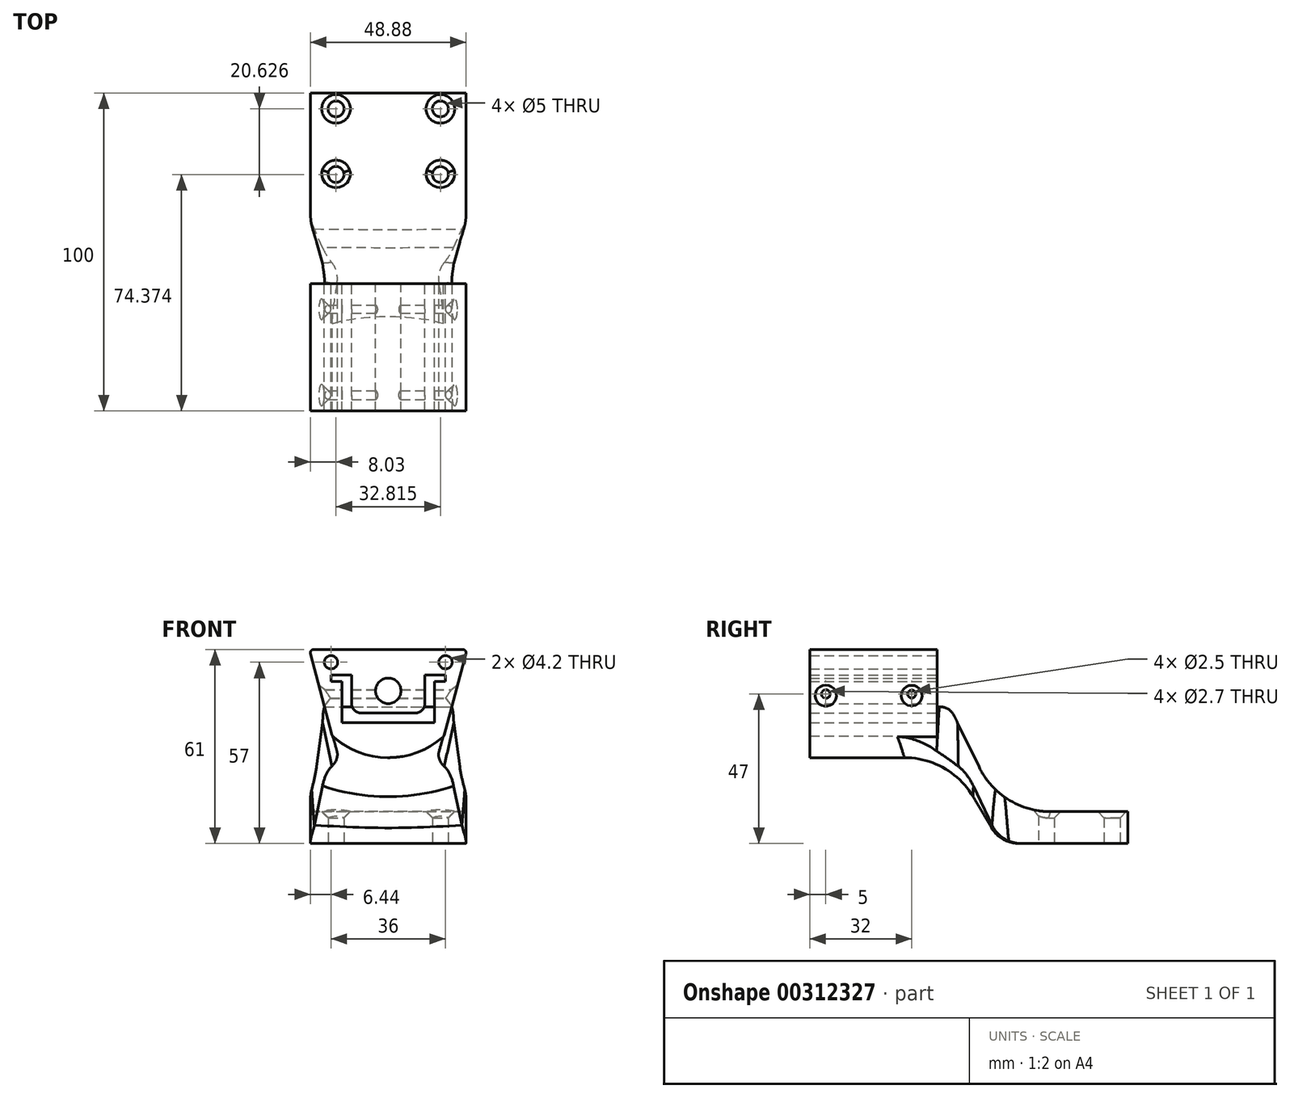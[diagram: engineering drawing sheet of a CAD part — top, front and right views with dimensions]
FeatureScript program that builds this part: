
annotation { "Feature Type Name" : "Feature", "Feature Type Description" : "" }
export const myFeature = defineFeature(function(context is Context, id is Id, definition is map)
    precondition{}
    {
        {
            var Q0;
            Q0=qCreatedBy(makeId("Front.planeOp"),FACE);
            var sketch = newSketch(context, id + "F0", { "sketchPlane" : qUnion([Q0])});
            skLineSegment(sketch, "E0", {"start": v(11.5, -9) * mm, "end": v(11.5, 0) * mm});
            skLineSegment(sketch, "E1", {"start": v(11.5, 0) * mm, "end": v(18, 0) * mm});
            skLineSegment(sketch, "E2", {"start": v(18, 0) * mm, "end": v(18, -2) * mm});
            skLineSegment(sketch, "E3", {"start": v(18, -2) * mm, "end": v(14.5, -2) * mm});
            skLineSegment(sketch, "E4", {"start": v(14.5, -2) * mm, "end": v(14.5, -15) * mm});
            skLineSegment(sketch, "E5", {"start": v(24.74, 8) * mm, "end": v(0.02, 8) * mm});
            skLineSegment(sketch, "E6.MirrorCS", {"start": v(-11.5, -9) * mm, "end": v(-11.5, 0) * mm});
            skLineSegment(sketch, "E7.MirrorCS", {"start": v(-11.5, 0) * mm, "end": v(-18, 0) * mm});
            skLineSegment(sketch, "E8.MirrorCS", {"start": v(-14.5, -2) * mm, "end": v(-14.5, -15) * mm});
            skLineSegment(sketch, "E9.MirrorCS", {"start": v(-14.98, 8) * mm, "end": v(0.02, 8) * mm});
            skLineSegment(sketch, "E10.MirrorCS", {"start": v(-18, 0) * mm, "end": v(-18, -2) * mm});
            skLineSegment(sketch, "E11.MirrorCS", {"start": v(-18, -2) * mm, "end": v(-14.5, -2) * mm});
            skPoint(sketch, "E12.visualSharp", {"position": v(11.5, -12) * mm});
            skArc(sketch, "E12.filletArc", {"start": v(8.5, -12) * mm, "mid": v(10.62, -11.12) * mm, "end": v(11.5, -9) * mm});
            skPoint(sketch, "E13.visualSharp", {"position": v(-11.5, -12) * mm});
            skArc(sketch, "E13.filletArc", {"start": v(-11.5, -9) * mm, "mid": v(-10.62, -11.12) * mm, "end": v(-8.5, -12) * mm});
            skPoint(sketch, "E14.visualSharp", {"position": v(-20.98, 8) * mm});
            skPoint(sketch, "E15.visualSharp", {"position": v(21.02, 8) * mm});
            skCircle(sketch, "E16", {"center": v(0, 0) * mm, "radius": 26 * mm, "construction": true});
            skLineSegment(sketch, "E17", {"start": v(17.5, -19.23) * mm, "end": v(24.74, 8) * mm});
            skLineSegment(sketch, "E18", {"start": v(-14.98, 8) * mm, "end": v(-24.74, 8) * mm});
            skLineSegment(sketch, "E19", {"start": v(-24.74, 8) * mm, "end": v(-17.64, -19.1) * mm});
            skLineSegment(sketch, "E20", {"start": v(-8.5, -12) * mm, "end": v(8.5, -12) * mm});
            skCircle(sketch, "E21", {"center": v(0, -5) * mm, "radius": 4 * mm});
            skCircle(sketch, "E22", {"center": v(-18, 4) * mm, "radius": 2.1 * mm});
            skCircle(sketch, "E23", {"center": v(18, 4) * mm, "radius": 2.1 * mm});
            skArc(sketch, "E24", {"start": v(17.5, -19.23) * mm, "mid": v(-0.1, -26) * mm, "end": v(-17.64, -19.1) * mm});
            skLineSegment(sketch, "E25", {"start": v(-14.5, -15) * mm, "end": v(14.5, -15) * mm});
            skSolve(sketch);
        }
        {
            var Q0;
            Q0=qSketchRegion(id+"F0",true);
            extrude(context, id + "F1", {"entities" : qUnion([Q0]), "depth" : 40 * mm});
        }
        {
            var Q0;
            Q0=qCreatedBy(makeId("Right.planeOp"),FACE);
            var sketch = newSketch(context, id + "F2", { "sketchPlane" : qUnion([Q0])});
            skCircle(sketch, "E26", {"center": v(-35, -6) * mm, "radius": 1.35 * mm});
            skCircle(sketch, "E27", {"center": v(-8, -6) * mm, "radius": 1.25 * mm});
            skSolve(sketch);
        }
        {
            var Q0;
            Q0=qSketchRegion(id+"F2",true);
            extrude(context, id + "F3", {"entities" : qUnion([Q0]), "operationType" : NewBodyOperationType.REMOVE, "endBound" : BoundingType.THROUGH_ALL, "oppositeDirection" : true, "depth" : 25 * mm, "hasSecondDirection" : true, "secondDirectionBound" : SecondDirectionBoundingType.THROUGH_ALL, "secondDirectionOppositeDirection" : false, "secondDirectionDepth" : 25 * mm});
        }
        {
            var Q0;
            Q0=makeQuery(id+"F3.boolean.opBoolean","INTERSECT",EDGE,{"derivedFrom":[makeQuery(id+"F1.opExtrude","SWEPT_FACE",FACE,{"disambiguationData":[OSD([sQuery(id+"F0.wireOp",EDGE,"E17")])]}),makeQuery(id+"F3.opExtrude","SWEPT_FACE",FACE,{"disambiguationData":[OSD([sQuery(id+"F2.wireOp",EDGE,"E26")])]})]});
            var Q1;
            Q1=makeQuery(id+"F3.boolean.opBoolean","INTERSECT",EDGE,{"derivedFrom":[makeQuery(id+"F1.opExtrude","SWEPT_FACE",FACE,{"disambiguationData":[OSD([sQuery(id+"F0.wireOp",EDGE,"E19")])]}),makeQuery(id+"F3.opExtrude","SWEPT_FACE",FACE,{"disambiguationData":[OSD([sQuery(id+"F2.wireOp",EDGE,"E26")])]})]});
            var Q2;
            Q2=makeQuery(id+"F3.boolean.opBoolean","INTERSECT",EDGE,{"derivedFrom":[makeQuery(id+"F1.opExtrude","SWEPT_FACE",FACE,{"disambiguationData":[OSD([sQuery(id+"F0.wireOp",EDGE,"E19")])]}),makeQuery(id+"F3.opExtrude","SWEPT_FACE",FACE,{"disambiguationData":[OSD([sQuery(id+"F2.wireOp",EDGE,"E27")])]})]});
            var Q3;
            Q3=makeQuery(id+"F3.boolean.opBoolean","INTERSECT",EDGE,{"derivedFrom":[makeQuery(id+"F1.opExtrude","SWEPT_FACE",FACE,{"disambiguationData":[OSD([sQuery(id+"F0.wireOp",EDGE,"E17")])]}),makeQuery(id+"F3.opExtrude","SWEPT_FACE",FACE,{"disambiguationData":[OSD([sQuery(id+"F2.wireOp",EDGE,"E27")])]})]});
            chamfer(context, id + "F4", {"entities" : qUnion([Q0, Q1, Q2, Q3]), "width" : 2 * mm, "tangentPropagation" : true});
        }
        {
            var Q0;
            Q0=makeQuery(id+"F1.opExtrude","SWEPT_EDGE",EDGE,{"disambiguationData":[OSD([sQuery(id+"F0.wireOp",EDGE,"E18"),sQuery(id+"F0.wireOp",EDGE,"E19")])]});
            var Q1;
            Q1=makeQuery(id+"F1.opExtrude","SWEPT_EDGE",EDGE,{"disambiguationData":[OSD([sQuery(id+"F0.wireOp",EDGE,"1d934c00-5e39-40e0-b069-677cc9a50368.MirrorCS"),sQuery(id+"F0.wireOp",EDGE,"E19")])]});
            var Q2;
            Q2=makeQuery(id+"F1.opExtrude","SWEPT_EDGE",EDGE,{"disambiguationData":[OSD([sQuery(id+"F0.wireOp",EDGE,"E5"),sQuery(id+"F0.wireOp",EDGE,"E17")])]});
            var Q3;
            Q3=makeQuery(id+"F1.opExtrude","SWEPT_EDGE",EDGE,{"disambiguationData":[OSD([sQuery(id+"F0.wireOp",EDGE,"bbf43ac0-3a89-452c-aa49-668b63ebcc61"),sQuery(id+"F0.wireOp",EDGE,"E17")])]});
            fillet(context, id + "F5", {"entities" : qUnion([Q0, Q1, Q2, Q3]), "radius" : 1 * mm, "tangentPropagation" : true, "allowEdgeOverflow" : false});
        }
        {
            var Q0;
            Q0=makeQuery(id+"F1.opExtrude","CAP_FACE",FACE,{"disambiguationData":[OSD([sQuery(id+"F0.wireOp",EDGE,"E0"),sQuery(id+"F0.wireOp",EDGE,"E1"),sQuery(id+"F0.wireOp",EDGE,"E2"),sQuery(id+"F0.wireOp",EDGE,"E3"),sQuery(id+"F0.wireOp",EDGE,"E4"),sQuery(id+"F0.wireOp",EDGE,"E5"),sQuery(id+"F0.wireOp",EDGE,"E6.MirrorCS"),sQuery(id+"F0.wireOp",EDGE,"E7.MirrorCS"),sQuery(id+"F0.wireOp",EDGE,"E8.MirrorCS"),sQuery(id+"F0.wireOp",EDGE,"E9.MirrorCS"),sQuery(id+"F0.wireOp",EDGE,"E10.MirrorCS"),sQuery(id+"F0.wireOp",EDGE,"E11.MirrorCS"),sQuery(id+"F0.wireOp",EDGE,"E12.filletArc"),sQuery(id+"F0.wireOp",EDGE,"E13.filletArc"),sQuery(id+"F0.wireOp",EDGE,"E17"),sQuery(id+"F0.wireOp",EDGE,"E18"),sQuery(id+"F0.wireOp",EDGE,"E19"),sQuery(id+"F0.wireOp",EDGE,"E20"),sQuery(id+"F0.wireOp",EDGE,"E21"),sQuery(id+"F0.wireOp",EDGE,"E22"),sQuery(id+"F0.wireOp",EDGE,"E23"),sQuery(id+"F0.wireOp",EDGE,"E24"),sQuery(id+"F0.wireOp",EDGE,"E25")])],"isStart":true});
            cPlane(context, id + "F6", {"entities" : qUnion([Q0]), "cplaneType" : CPlaneType.OFFSET, "offset" : 20 * mm, "width" : 150 * mm, "height" : 150 * mm});
        }
        {
            var Q0;
            Q0=qCreatedBy(id+"F6.planeOp",FACE);
            var sketch = newSketch(context, id + "F7", { "sketchPlane" : qUnion([Q0])});
            skLineSegment(sketch, "E28.bottom", {"start": v(-24.4, -43) * mm, "end": v(24.41, -43) * mm});
            skLineSegment(sketch, "E28.top", {"start": v(-24.4, -53) * mm, "end": v(24.41, -53) * mm});
            skLineSegment(sketch, "E28.left", {"start": v(-24.4, -43) * mm, "end": v(-24.4, -53) * mm});
            skLineSegment(sketch, "E28.right", {"start": v(24.41, -43) * mm, "end": v(24.41, -53) * mm});
            skSolve(sketch);
        }
        {
            var Q0;
            Q0=makeQuery(id+"F1.opExtrude","CAP_FACE",FACE,{"disambiguationData":[OSD([sQuery(id+"F0.wireOp",EDGE,"E0"),sQuery(id+"F0.wireOp",EDGE,"E1"),sQuery(id+"F0.wireOp",EDGE,"E2"),sQuery(id+"F0.wireOp",EDGE,"E3"),sQuery(id+"F0.wireOp",EDGE,"E4"),sQuery(id+"F0.wireOp",EDGE,"E5"),sQuery(id+"F0.wireOp",EDGE,"E6.MirrorCS"),sQuery(id+"F0.wireOp",EDGE,"E7.MirrorCS"),sQuery(id+"F0.wireOp",EDGE,"E8.MirrorCS"),sQuery(id+"F0.wireOp",EDGE,"E9.MirrorCS"),sQuery(id+"F0.wireOp",EDGE,"E10.MirrorCS"),sQuery(id+"F0.wireOp",EDGE,"E11.MirrorCS"),sQuery(id+"F0.wireOp",EDGE,"E12.filletArc"),sQuery(id+"F0.wireOp",EDGE,"E13.filletArc"),sQuery(id+"F0.wireOp",EDGE,"E17"),sQuery(id+"F0.wireOp",EDGE,"E18"),sQuery(id+"F0.wireOp",EDGE,"E19"),sQuery(id+"F0.wireOp",EDGE,"E20"),sQuery(id+"F0.wireOp",EDGE,"E21"),sQuery(id+"F0.wireOp",EDGE,"E22"),sQuery(id+"F0.wireOp",EDGE,"E23"),sQuery(id+"F0.wireOp",EDGE,"E24"),sQuery(id+"F0.wireOp",EDGE,"E25")])],"isStart":true});
            var sketch = newSketch(context, id + "F8", { "sketchPlane" : qUnion([Q0])});
            skArc(sketch, "E29", {"start": v(-17.27, -19.43) * mm, "mid": v(0.1, -26) * mm, "end": v(17.42, -19.3) * mm});
            skLineSegment(sketch, "E30", {"start": v(17.42, -19.3) * mm, "end": v(20.03, -10) * mm});
            skLineSegment(sketch, "E31", {"start": v(20.03, -10) * mm, "end": v(-19.95, -10) * mm});
            skLineSegment(sketch, "E32", {"start": v(-19.95, -10) * mm, "end": v(-17.27, -19.43) * mm});
            skSolve(sketch);
        }
        {
            var Q0;
            Q0=qSketchRegion(id+"F8",true);
            extrude(context, id + "F9", {"entities" : qUnion([Q0]), "operationType" : NewBodyOperationType.ADD, "depth" : 4 * mm});
        }
        {
            var Q1;
            Q1=makeQuery(id+"F9.opExtrude","CAP_FACE",FACE,{"disambiguationData":[OSD([sQuery(id+"F8.wireOp",EDGE,"E29"),sQuery(id+"F8.wireOp",EDGE,"E30"),sQuery(id+"F8.wireOp",EDGE,"E31"),sQuery(id+"F8.wireOp",EDGE,"E32")])],"isStart":false});
            var Q2;
            Q2=qSketchRegion(id+"F7",true);
            loft(context, id + "F10", {"operationType" : NewBodyOperationType.ADD, "sheetProfilesArray" : [{ "sheetProfileEntities" : qUnion([Q1]) }, { "sheetProfileEntities" : qUnion([Q2]) }]});
        }
        {
            var Q0;
            {var subQ0=sQuery(id+"F8.wireOp",EDGE,"E29");Q0=makeQuery(id+"F10.boolean.opBoolean","MERGE",EDGE,{"derivedFrom":[makeQuery(id+"F9.opExtrude","CAP_EDGE",EDGE,{"disambiguationData":[OSD([subQ0])],"isStart":false}),makeQuery(id+"F10.opLoft","MID_CAP_EDGE",EDGE,{"disambiguationData":[OSD([sQuery(id+"F0.wireOp",EDGE,"E0"),sQuery(id+"F0.wireOp",EDGE,"E1"),sQuery(id+"F0.wireOp",EDGE,"E2"),sQuery(id+"F0.wireOp",EDGE,"E3"),sQuery(id+"F0.wireOp",EDGE,"E4"),sQuery(id+"F0.wireOp",EDGE,"E5"),sQuery(id+"F0.wireOp",EDGE,"E6.MirrorCS"),sQuery(id+"F0.wireOp",EDGE,"E7.MirrorCS"),sQuery(id+"F0.wireOp",EDGE,"E8.MirrorCS"),sQuery(id+"F0.wireOp",EDGE,"E9.MirrorCS"),sQuery(id+"F0.wireOp",EDGE,"E10.MirrorCS"),sQuery(id+"F0.wireOp",EDGE,"E11.MirrorCS"),sQuery(id+"F0.wireOp",EDGE,"E12.filletArc"),sQuery(id+"F0.wireOp",EDGE,"E13.filletArc"),sQuery(id+"F0.wireOp",EDGE,"E17"),sQuery(id+"F0.wireOp",EDGE,"E18"),sQuery(id+"F0.wireOp",EDGE,"E19"),sQuery(id+"F0.wireOp",EDGE,"E20"),sQuery(id+"F0.wireOp",EDGE,"E21"),sQuery(id+"F0.wireOp",EDGE,"E22"),sQuery(id+"F0.wireOp",EDGE,"E23"),sQuery(id+"F0.wireOp",EDGE,"E24"),sQuery(id+"F0.wireOp",EDGE,"E25"),subQ0,sQuery(id+"F8.wireOp",EDGE,"E30"),sQuery(id+"F8.wireOp",EDGE,"E32")])],"capPos":0.0})]});}
            fillet(context, id + "F11", {"entities" : qUnion([Q0]), "radius" : 25 * mm, "tangentPropagation" : true, "allowEdgeOverflow" : false});
        }
        {
            var Q0;
            Q0=makeQuery(id+"F10.opLoft","CAP_FACE",FACE,{"disambiguationData":[OSD([makeQuery(id+"F7.imprint","IMPRINT",FACE,{"disambiguationData":[TD([[makeQuery(id+"F7.imprint","IMPRINT",EDGE,{"derivedFrom":sQuery(id+"F7.wireOp",EDGE,"E28.bottom")}),-1.0]])]})])],"isStart":true});
            extrude(context, id + "F12", {"entities" : qUnion([Q0]), "operationType" : NewBodyOperationType.ADD, "depth" : 40 * mm});
        }
        {
            var Q0;
            {var subQ0=sQuery(id+"F7.wireOp",EDGE,"E28.right");var subQ1=sQuery(id+"F7.wireOp",EDGE,"E28.left");var subQ2=sQuery(id+"F7.wireOp",EDGE,"E28.bottom");Q0=makeQuery(id+"F12.boolean.opBoolean","MERGE",EDGE,{"derivedFrom":[makeQuery(id+"F10.opLoft","MID_CAP_EDGE",EDGE,{"disambiguationData":[OSD([subQ2,subQ1,subQ0])],"capPos":1.0}),makeQuery(id+"F12.opExtrude","CAP_EDGE",EDGE,{"disambiguationData":[OSD([subQ2,subQ1,subQ0])],"isStart":true})]});}
            fillet(context, id + "F13", {"entities" : qUnion([Q0]), "radius" : 25 * mm, "tangentPropagation" : true, "allowEdgeOverflow" : false});
        }
        {
            var Q0;
            {var subQ0=sQuery(id+"F8.wireOp",EDGE,"E32");Q0=makeQuery(id+"F10.boolean.opBoolean","MERGE",EDGE,{"derivedFrom":[makeQuery(id+"F9.opExtrude","CAP_EDGE",EDGE,{"disambiguationData":[OSD([subQ0])],"isStart":false}),makeQuery(id+"F10.opLoft","MID_CAP_EDGE",EDGE,{"disambiguationData":[OSD([sQuery(id+"F0.wireOp",EDGE,"E0"),sQuery(id+"F0.wireOp",EDGE,"E1"),sQuery(id+"F0.wireOp",EDGE,"E2"),sQuery(id+"F0.wireOp",EDGE,"E3"),sQuery(id+"F0.wireOp",EDGE,"E4"),sQuery(id+"F0.wireOp",EDGE,"E5"),sQuery(id+"F0.wireOp",EDGE,"E6.MirrorCS"),sQuery(id+"F0.wireOp",EDGE,"E7.MirrorCS"),sQuery(id+"F0.wireOp",EDGE,"E8.MirrorCS"),sQuery(id+"F0.wireOp",EDGE,"E9.MirrorCS"),sQuery(id+"F0.wireOp",EDGE,"E10.MirrorCS"),sQuery(id+"F0.wireOp",EDGE,"E11.MirrorCS"),sQuery(id+"F0.wireOp",EDGE,"E12.filletArc"),sQuery(id+"F0.wireOp",EDGE,"E13.filletArc"),sQuery(id+"F0.wireOp",EDGE,"E17"),sQuery(id+"F0.wireOp",EDGE,"E18"),sQuery(id+"F0.wireOp",EDGE,"E19"),sQuery(id+"F0.wireOp",EDGE,"E20"),sQuery(id+"F0.wireOp",EDGE,"E21"),sQuery(id+"F0.wireOp",EDGE,"E22"),sQuery(id+"F0.wireOp",EDGE,"E23"),sQuery(id+"F0.wireOp",EDGE,"E24"),sQuery(id+"F0.wireOp",EDGE,"E25"),sQuery(id+"F8.wireOp",EDGE,"E29"),sQuery(id+"F8.wireOp",EDGE,"E31"),subQ0])],"capPos":0.0})]});}
            var Q1;
            {var subQ0=sQuery(id+"F7.wireOp",EDGE,"E28.right");var subQ1=sQuery(id+"F7.wireOp",EDGE,"E28.left");var subQ2=sQuery(id+"F7.wireOp",EDGE,"E28.top");Q1=makeQuery(id+"F12.boolean.opBoolean","MERGE",EDGE,{"derivedFrom":[makeQuery(id+"F10.opLoft","MID_CAP_EDGE",EDGE,{"disambiguationData":[OSD([subQ2,subQ1,subQ0])],"capPos":1.0}),makeQuery(id+"F12.opExtrude","CAP_EDGE",EDGE,{"disambiguationData":[OSD([subQ2,subQ1,subQ0])],"isStart":true})]});}
            var Q2;
            {var subQ0=sQuery(id+"F7.wireOp",EDGE,"E28.left");var subQ1=sQuery(id+"F7.wireOp",EDGE,"E28.top");var subQ2=sQuery(id+"F7.wireOp",EDGE,"E28.bottom");Q2=makeQuery(id+"F12.boolean.opBoolean","MERGE",EDGE,{"derivedFrom":[makeQuery(id+"F10.opLoft","MID_CAP_EDGE",EDGE,{"disambiguationData":[OSD([subQ2,subQ1,subQ0])],"capPos":1.0}),makeQuery(id+"F12.opExtrude","CAP_EDGE",EDGE,{"disambiguationData":[OSD([subQ2,subQ1,subQ0])],"isStart":true})]});}
            var Q3;
            {var subQ0=sQuery(id+"F7.wireOp",EDGE,"E28.right");var subQ1=sQuery(id+"F7.wireOp",EDGE,"E28.top");var subQ2=sQuery(id+"F7.wireOp",EDGE,"E28.bottom");Q3=makeQuery(id+"F12.boolean.opBoolean","MERGE",EDGE,{"derivedFrom":[makeQuery(id+"F10.opLoft","MID_CAP_EDGE",EDGE,{"disambiguationData":[OSD([subQ2,subQ1,subQ0])],"capPos":1.0}),makeQuery(id+"F12.opExtrude","CAP_EDGE",EDGE,{"disambiguationData":[OSD([subQ2,subQ1,subQ0])],"isStart":true})]});}
            var Q4;
            {var subQ0=sQuery(id+"F8.wireOp",EDGE,"E30");Q4=makeQuery(id+"F10.boolean.opBoolean","MERGE",EDGE,{"derivedFrom":[makeQuery(id+"F9.opExtrude","CAP_EDGE",EDGE,{"disambiguationData":[OSD([subQ0])],"isStart":false}),makeQuery(id+"F10.opLoft","MID_CAP_EDGE",EDGE,{"disambiguationData":[OSD([sQuery(id+"F0.wireOp",EDGE,"E0"),sQuery(id+"F0.wireOp",EDGE,"E1"),sQuery(id+"F0.wireOp",EDGE,"E2"),sQuery(id+"F0.wireOp",EDGE,"E3"),sQuery(id+"F0.wireOp",EDGE,"E4"),sQuery(id+"F0.wireOp",EDGE,"E5"),sQuery(id+"F0.wireOp",EDGE,"E6.MirrorCS"),sQuery(id+"F0.wireOp",EDGE,"E7.MirrorCS"),sQuery(id+"F0.wireOp",EDGE,"E8.MirrorCS"),sQuery(id+"F0.wireOp",EDGE,"E9.MirrorCS"),sQuery(id+"F0.wireOp",EDGE,"E10.MirrorCS"),sQuery(id+"F0.wireOp",EDGE,"E11.MirrorCS"),sQuery(id+"F0.wireOp",EDGE,"E12.filletArc"),sQuery(id+"F0.wireOp",EDGE,"E13.filletArc"),sQuery(id+"F0.wireOp",EDGE,"E17"),sQuery(id+"F0.wireOp",EDGE,"E18"),sQuery(id+"F0.wireOp",EDGE,"E19"),sQuery(id+"F0.wireOp",EDGE,"E20"),sQuery(id+"F0.wireOp",EDGE,"E21"),sQuery(id+"F0.wireOp",EDGE,"E22"),sQuery(id+"F0.wireOp",EDGE,"E23"),sQuery(id+"F0.wireOp",EDGE,"E24"),sQuery(id+"F0.wireOp",EDGE,"E25"),sQuery(id+"F8.wireOp",EDGE,"E29"),subQ0,sQuery(id+"F8.wireOp",EDGE,"E31")])],"capPos":0.0})]});}
            var Q5;
            {var subQ0=sQuery(id+"F0.wireOp",EDGE,"E25");var subQ1=sQuery(id+"F0.wireOp",EDGE,"E24");var subQ2=sQuery(id+"F0.wireOp",EDGE,"E23");var subQ3=sQuery(id+"F0.wireOp",EDGE,"E22");var subQ4=sQuery(id+"F0.wireOp",EDGE,"E21");var subQ5=sQuery(id+"F0.wireOp",EDGE,"E20");var subQ6=sQuery(id+"F0.wireOp",EDGE,"E19");var subQ7=sQuery(id+"F0.wireOp",EDGE,"E18");var subQ8=sQuery(id+"F0.wireOp",EDGE,"E17");var subQ9=sQuery(id+"F0.wireOp",EDGE,"E13.filletArc");var subQ10=sQuery(id+"F0.wireOp",EDGE,"E12.filletArc");var subQ11=sQuery(id+"F0.wireOp",EDGE,"E11.MirrorCS");var subQ12=sQuery(id+"F0.wireOp",EDGE,"E10.MirrorCS");var subQ13=sQuery(id+"F0.wireOp",EDGE,"E9.MirrorCS");var subQ14=sQuery(id+"F0.wireOp",EDGE,"E8.MirrorCS");var subQ15=sQuery(id+"F0.wireOp",EDGE,"E7.MirrorCS");var subQ16=sQuery(id+"F0.wireOp",EDGE,"E6.MirrorCS");var subQ17=sQuery(id+"F0.wireOp",EDGE,"E5");var subQ18=sQuery(id+"F0.wireOp",EDGE,"E4");var subQ19=sQuery(id+"F0.wireOp",EDGE,"E3");var subQ20=sQuery(id+"F0.wireOp",EDGE,"E2");var subQ21=sQuery(id+"F0.wireOp",EDGE,"E1");var subQ22=sQuery(id+"F0.wireOp",EDGE,"E0");Q5=makeQuery(id+"F11.opFillet","TWEAK_EDGE",EDGE,{"derivedFrom":[makeQuery(id+"F9.boolean.opBoolean","MERGE",VERTEX,{"derivedFrom":[makeQuery(id+"F5.opFillet","BLEND_VERTEX",VERTEX,{"blendedFrom":[makeQuery(id+"F1.opExtrude","SWEPT_EDGE",EDGE,{"disambiguationData":[OSD([subQ6,subQ1])]}),makeQuery(id+"F1.opExtrude","CAP_FACE",FACE,{"disambiguationData":[OSD([subQ22,subQ21,subQ20,subQ19,subQ18,subQ17,subQ16,subQ15,subQ14,subQ13,subQ12,subQ11,subQ10,subQ9,subQ8,subQ7,subQ6,subQ5,subQ4,subQ3,subQ2,subQ1,subQ0])],"isStart":true}),makeQuery(id+"F1.opExtrude","SWEPT_FACE",FACE,{"disambiguationData":[OSD([subQ1])]})],"blendedInto":[makeQuery(id+"F1.opExtrude","CAP_FACE",FACE,{"disambiguationData":[OSD([subQ22,subQ21,subQ20,subQ19,subQ18,subQ17,subQ16,subQ15,subQ14,subQ13,subQ12,subQ11,subQ10,subQ9,subQ8,subQ7,subQ6,subQ5,subQ4,subQ3,subQ2,subQ1,subQ0])],"isStart":true}),makeQuery(id+"F1.opExtrude","SWEPT_FACE",FACE,{"disambiguationData":[OSD([subQ1])]})]}),makeQuery(id+"F9.opExtrude","CAP_VERTEX",VERTEX,{"disambiguationData":[OSD([subQ22,subQ21,subQ20,subQ19,subQ18,subQ17,subQ16,subQ15,subQ14,subQ13,subQ12,subQ11,subQ10,subQ9,subQ8,subQ7,subQ6,subQ5,subQ4,subQ3,subQ2,subQ1,subQ0,sQuery(id+"F8.wireOp",EDGE,"E29"),sQuery(id+"F8.wireOp",EDGE,"E30")])],"isStart":true})]})]});}
            fillet(context, id + "F14", {"entities" : qUnion([Q0, Q1, Q2, Q3, Q4, Q5]), "radius" : 10 * mm, "tangentPropagation" : true, "allowEdgeOverflow" : false});
        }
        {
            var Q0;
            {var subQ0=sQuery(id+"F8.wireOp",EDGE,"E31");Q0=makeQuery(id+"F10.boolean.opBoolean","MERGE",EDGE,{"derivedFrom":[makeQuery(id+"F9.opExtrude","CAP_EDGE",EDGE,{"disambiguationData":[OSD([subQ0])],"isStart":false}),makeQuery(id+"F10.opLoft","MID_CAP_EDGE",EDGE,{"disambiguationData":[OSD([sQuery(id+"F0.wireOp",EDGE,"E17"),sQuery(id+"F0.wireOp",EDGE,"E19"),sQuery(id+"F8.wireOp",EDGE,"E30"),subQ0,sQuery(id+"F8.wireOp",EDGE,"E32")])],"capPos":0.0})]});}
            fillet(context, id + "F15", {"entities" : qUnion([Q0]), "radius" : 5 * mm, "tangentPropagation" : true, "allowEdgeOverflow" : false});
        }
        {
            var Q0;
            Q0=makeQuery(id+"F12.opExtrude","SWEPT_FACE",FACE,{"disambiguationData":[OSD([sQuery(id+"F7.wireOp",EDGE,"E28.top"),sQuery(id+"F7.wireOp",EDGE,"E28.left"),sQuery(id+"F7.wireOp",EDGE,"E28.right")])]});
            var sketch = newSketch(context, id + "F16", { "sketchPlane" : qUnion([Q0])});
            skCircle(sketch, "E33", {"center": v(-16.41, -34.38) * mm, "radius": 2.5 * mm});
            skCircle(sketch, "E34", {"center": v(16.4, -34.37) * mm, "radius": 2.5 * mm});
            skCircle(sketch, "E35", {"center": v(16.4, -55) * mm, "radius": 2.5 * mm});
            skCircle(sketch, "E36", {"center": v(-16.41, -55) * mm, "radius": 2.5 * mm});
            skSolve(sketch);
        }
        {
            var Q0;
            Q0=qSketchRegion(id+"F16",true);
            extrude(context, id + "F17", {"entities" : qUnion([Q0]), "operationType" : NewBodyOperationType.REMOVE, "endBound" : BoundingType.THROUGH_ALL, "oppositeDirection" : true, "depth" : 25 * mm});
        }
        {
            var Q0;
            Q0=makeQuery(id+"F17.boolean.opBoolean","INTERSECT",EDGE,{"derivedFrom":[makeQuery(id+"F13.opFillet","BLEND_FACE",FACE,{"disambiguationData":[OSD([sQuery(id+"F7.wireOp",EDGE,"E28.bottom"),sQuery(id+"F7.wireOp",EDGE,"E28.left"),sQuery(id+"F7.wireOp",EDGE,"E28.right")])]}),makeQuery(id+"F17.opExtrude","SWEPT_FACE",FACE,{"disambiguationData":[OSD([sQuery(id+"F16.wireOp",EDGE,"E33")])]})]});
            var Q1;
            Q1=makeQuery(id+"F17.boolean.opBoolean","INTERSECT",EDGE,{"derivedFrom":[makeQuery(id+"F12.opExtrude","SWEPT_FACE",FACE,{"disambiguationData":[OSD([sQuery(id+"F7.wireOp",EDGE,"E28.bottom"),sQuery(id+"F7.wireOp",EDGE,"E28.left"),sQuery(id+"F7.wireOp",EDGE,"E28.right")])]}),makeQuery(id+"F17.opExtrude","SWEPT_FACE",FACE,{"disambiguationData":[OSD([sQuery(id+"F16.wireOp",EDGE,"E33")])]})]});
            var Q2;
            Q2=makeQuery(id+"F17.boolean.opBoolean","INTERSECT",EDGE,{"derivedFrom":[makeQuery(id+"F12.opExtrude","SWEPT_FACE",FACE,{"disambiguationData":[OSD([sQuery(id+"F7.wireOp",EDGE,"E28.bottom"),sQuery(id+"F7.wireOp",EDGE,"E28.left"),sQuery(id+"F7.wireOp",EDGE,"E28.right")])]}),makeQuery(id+"F17.opExtrude","SWEPT_FACE",FACE,{"disambiguationData":[OSD([sQuery(id+"F16.wireOp",EDGE,"E36")])]})]});
            var Q3;
            Q3=makeQuery(id+"F17.boolean.opBoolean","INTERSECT",EDGE,{"derivedFrom":[makeQuery(id+"F13.opFillet","BLEND_FACE",FACE,{"disambiguationData":[OSD([sQuery(id+"F7.wireOp",EDGE,"E28.bottom"),sQuery(id+"F7.wireOp",EDGE,"E28.left"),sQuery(id+"F7.wireOp",EDGE,"E28.right")])]}),makeQuery(id+"F17.opExtrude","SWEPT_FACE",FACE,{"disambiguationData":[OSD([sQuery(id+"F16.wireOp",EDGE,"E34")])]})]});
            var Q4;
            Q4=makeQuery(id+"F17.boolean.opBoolean","INTERSECT",EDGE,{"derivedFrom":[makeQuery(id+"F12.opExtrude","SWEPT_FACE",FACE,{"disambiguationData":[OSD([sQuery(id+"F7.wireOp",EDGE,"E28.bottom"),sQuery(id+"F7.wireOp",EDGE,"E28.left"),sQuery(id+"F7.wireOp",EDGE,"E28.right")])]}),makeQuery(id+"F17.opExtrude","SWEPT_FACE",FACE,{"disambiguationData":[OSD([sQuery(id+"F16.wireOp",EDGE,"E35")])]})]});
            chamfer(context, id + "F18", {"entities" : qUnion([Q0, Q1, Q2, Q3, Q4]), "width" : 2 * mm, "tangentPropagation" : true});
        }
    });
